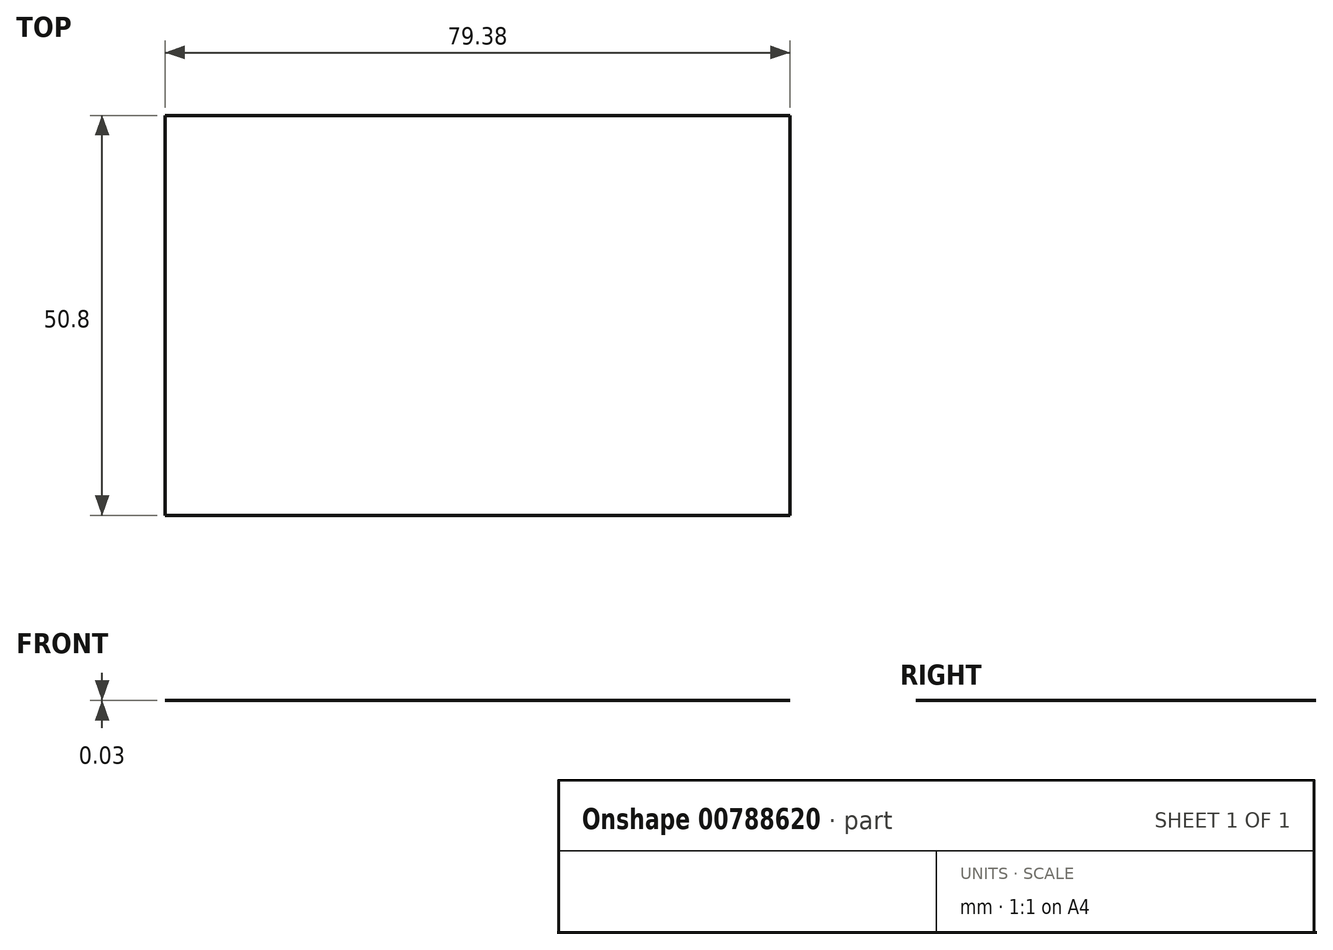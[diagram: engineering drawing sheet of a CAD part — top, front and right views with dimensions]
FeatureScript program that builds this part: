
annotation { "Feature Type Name" : "Feature", "Feature Type Description" : "" }
export const myFeature = defineFeature(function(context is Context, id is Id, definition is map)
    precondition{}
    {
        {
            var Q0;
            Q0=qCreatedBy(makeId("Top.planeOp"),FACE);
            var sketch = newSketch(context, id + "F0", { "sketchPlane" : qUnion([Q0])});
            skLineSegment(sketch, "E0.bottom", {"start": v(0, 0) * mm, "end": v(79.38, 0) * mm});
            skLineSegment(sketch, "E0.top", {"start": v(0, 50.8) * mm, "end": v(79.37, 50.8) * mm});
            skLineSegment(sketch, "E0.left", {"start": v(0, 0) * mm, "end": v(0, 50.8) * mm});
            skLineSegment(sketch, "E0.right", {"start": v(79.38, 0) * mm, "end": v(79.37, 50.8) * mm});
            skSolve(sketch);
        }
        {
            var Q0;
            Q0=qSketchRegion(id+"F0",true);
            extrude(context, id + "F1", {"entities" : qUnion([Q0]), "depth" : 3 / 101.6 * mm, "offsetDistance" : 25.4 * mm});
        }
    });
